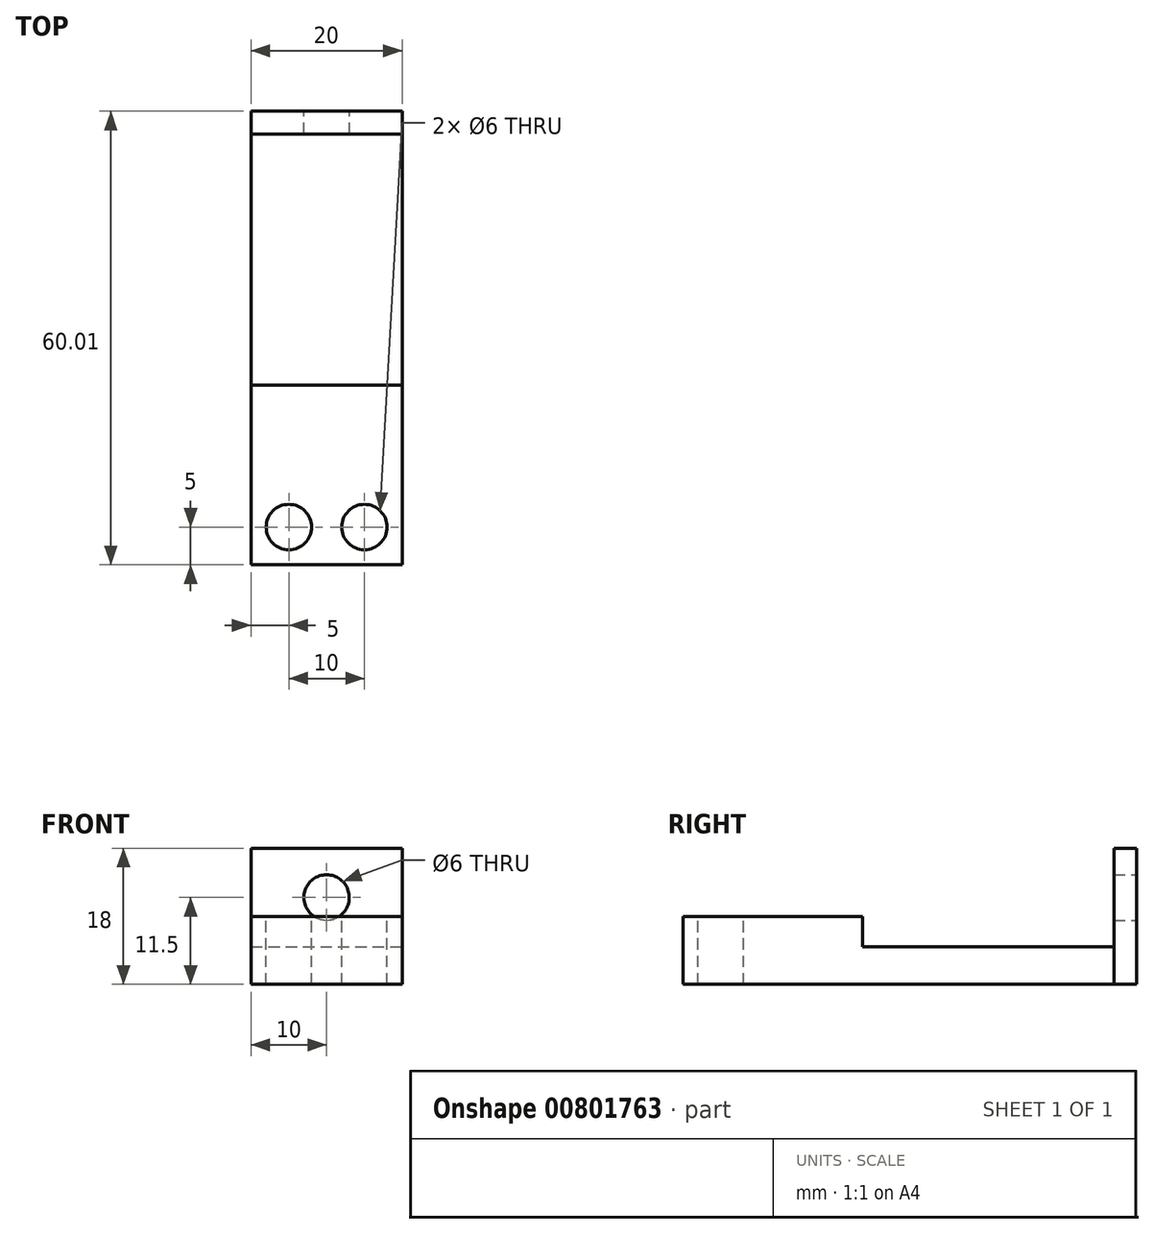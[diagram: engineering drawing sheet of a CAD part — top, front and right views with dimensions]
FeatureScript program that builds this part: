
annotation { "Feature Type Name" : "Feature", "Feature Type Description" : "" }
export const myFeature = defineFeature(function(context is Context, id is Id, definition is map)
    precondition{}
    {
        {
            var Q0;
            Q0=qCreatedBy(makeId("Top.planeOp"),FACE);
            var sketch = newSketch(context, id + "F0", { "sketchPlane" : qUnion([Q0])});
            skLineSegment(sketch, "E0.bottom", {"start": v(0, 0) * mm, "end": v(20, 0) * mm});
            skLineSegment(sketch, "E0.top", {"start": v(0, 57) * mm, "end": v(20, 57) * mm});
            skLineSegment(sketch, "E0.left", {"start": v(0, 0) * mm, "end": v(0, 57) * mm});
            skLineSegment(sketch, "E0.right", {"start": v(20, 0) * mm, "end": v(20, 57) * mm});
            skSolve(sketch);
        }
        {
            var Q0;
            Q0 = qSketchRegion(id + "F0", true);
            extrude(context, id + "F1", {"entities" : qUnion([Q0]), "depth" : 5 * mm, "offsetDistance" : 25 * mm});
        }
        {
            var Q0;
            Q0=qCreatedBy(makeId("Top.planeOp"),FACE);
            var sketch = newSketch(context, id + "F2", { "sketchPlane" : qUnion([Q0])});
            skLineSegment(sketch, "E1.bottom", {"start": v(0, 57.01) * mm, "end": v(20, 57.01) * mm});
            skLineSegment(sketch, "E1.top", {"start": v(0, 60.01) * mm, "end": v(20, 60.01) * mm});
            skLineSegment(sketch, "E1.left", {"start": v(0, 57.01) * mm, "end": v(0, 60.01) * mm});
            skLineSegment(sketch, "E1.right", {"start": v(20, 57.01) * mm, "end": v(20, 60.01) * mm});
            skSolve(sketch);
        }
        {
            var Q0;
            Q0=makeQuery(id+"F2.imprint","IMPRINT",FACE,{"disambiguationData":[TD([[makeQuery(id+"F2.imprint","IMPRINT",EDGE,{"derivedFrom":sQuery(id+"F2.wireOp",EDGE,"E1.bottom")}),1.0]])]});
            extrude(context, id + "F3", {"entities" : qUnion([Q0]), "depth" : 18 * mm, "offsetDistance" : 25 * mm});
        }
        {
            var Q0;
            Q0=makeQuery(id+"F3.opExtrude","SWEPT_FACE",FACE,{"disambiguationData":[OSD([sQuery(id+"F2.wireOp",EDGE,"E1.top")])]});
            var sketch = newSketch(context, id + "F4", { "sketchPlane" : qUnion([Q0])});
            skCircle(sketch, "E2", {"center": v(-10, 11.5) * mm, "radius": 3 * mm});
            skSolve(sketch);
        }
        {
            var Q0;
            Q0=makeQuery(id+"F4.imprint","IMPRINT",FACE,{"disambiguationData":[TD([[makeQuery(id+"F4.imprint","IMPRINT",EDGE,{"derivedFrom":sQuery(id+"F4.wireOp",EDGE,"E2")}),1.0]])]});
            extrude(context, id + "F5", {"entities" : qUnion([Q0]), "operationType" : NewBodyOperationType.REMOVE, "oppositeDirection" : true, "depth" : 10 * mm, "offsetDistance" : 25 * mm});
        }
        {
            var Q0;
            Q0=makeQuery(id+"F1.opExtrude","CAP_FACE",FACE,{"disambiguationData":[OSD([sQuery(id+"F0.wireOp",EDGE,"E0.bottom"),sQuery(id+"F0.wireOp",EDGE,"E0.top"),sQuery(id+"F0.wireOp",EDGE,"E0.left"),sQuery(id+"F0.wireOp",EDGE,"E0.right")])],"isStart":false});
            var sketch = newSketch(context, id + "F6", { "sketchPlane" : qUnion([Q0])});
            skLineSegment(sketch, "E3.bottom", {"start": v(0, 0) * mm, "end": v(20, 0) * mm});
            skLineSegment(sketch, "E3.top", {"start": v(0, 23.75) * mm, "end": v(20, 23.75) * mm});
            skLineSegment(sketch, "E3.left", {"start": v(0, 0) * mm, "end": v(0, 23.75) * mm});
            skLineSegment(sketch, "E3.right", {"start": v(20, 0) * mm, "end": v(20, 13.94) * mm});
            skSolve(sketch);
        }
        {
            var Q0;
            Q0=makeQuery(id+"F6.imprint","IMPRINT",FACE,{"disambiguationData":[TD([[makeQuery(id+"F6.imprint","IMPRINT",EDGE,{"derivedFrom":sQuery(id+"F6.wireOp",EDGE,"E3.bottom")}),1.0]])]});
            extrude(context, id + "F7", {"entities" : qUnion([Q0]), "operationType" : NewBodyOperationType.ADD, "depth" : 4 * mm, "offsetDistance" : 25 * mm});
        }
        {
            var Q0;
            Q0=makeQuery(id+"F7.opExtrude","CAP_FACE",FACE,{"disambiguationData":[OSD([sQuery(id+"F0.wireOp",EDGE,"E0.right"),sQuery(id+"F6.wireOp",EDGE,"E3.bottom"),sQuery(id+"F6.wireOp",EDGE,"E3.top"),sQuery(id+"F6.wireOp",EDGE,"E3.left"),sQuery(id+"F6.wireOp",EDGE,"E3.right")])],"isStart":false});
            var sketch = newSketch(context, id + "F8", { "sketchPlane" : qUnion([Q0])});
            skCircle(sketch, "E4", {"center": v(5, 5) * mm, "radius": 3 * mm});
            skCircle(sketch, "E5.1.0.0", {"center": v(15, 5) * mm, "radius": 3 * mm});
            skLineSegment(sketch, "E5.direction1", {"start": v(5, 5) * mm, "end": v(15, 5) * mm, "construction": true});
            skSolve(sketch);
        }
        {
            var Q0;
            Q0=makeQuery(id+"F8.imprint","IMPRINT",FACE,{"disambiguationData":[TD([[makeQuery(id+"F8.imprint","IMPRINT",EDGE,{"derivedFrom":sQuery(id+"F8.wireOp",EDGE,"E4")}),1.0]])]});
            var Q1;
            Q1=makeQuery(id+"F8.imprint","IMPRINT",FACE,{"disambiguationData":[TD([[makeQuery(id+"F8.imprint","IMPRINT",EDGE,{"derivedFrom":sQuery(id+"F8.wireOp",EDGE,"E5.1.0.0")}),1.0]])]});
            extrude(context, id + "F9", {"entities" : qUnion([Q0, Q1]), "operationType" : NewBodyOperationType.REMOVE, "oppositeDirection" : true, "depth" : 25 * mm, "offsetDistance" : 25 * mm});
        }
    });
